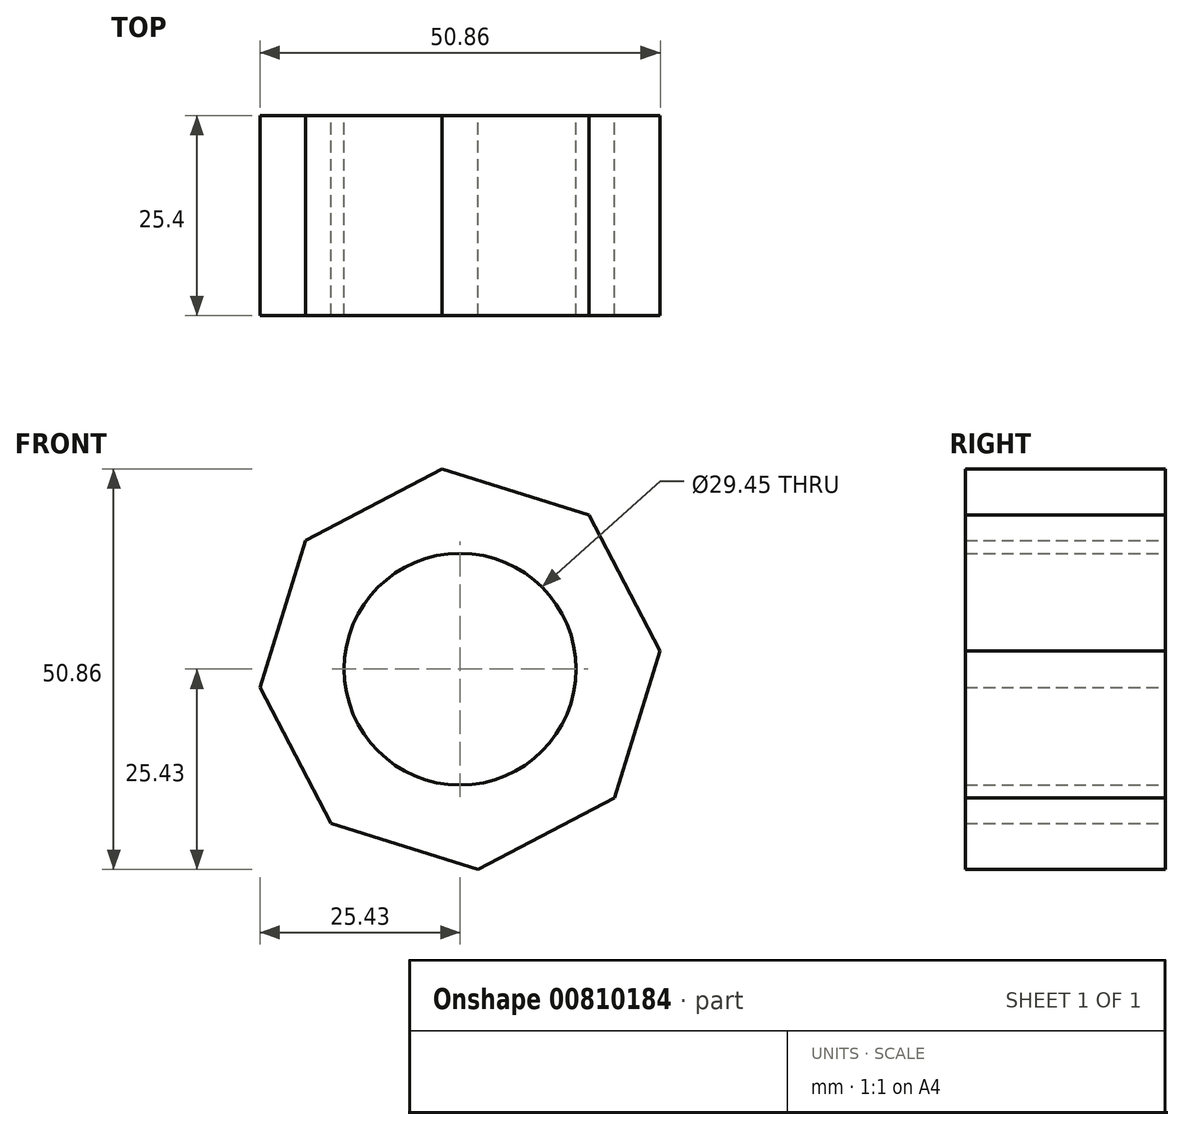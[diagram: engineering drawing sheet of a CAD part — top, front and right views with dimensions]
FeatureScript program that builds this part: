
annotation { "Feature Type Name" : "Feature", "Feature Type Description" : "" }
export const myFeature = defineFeature(function(context is Context, id is Id, definition is map)
    precondition{}
    {
        {
            var Q0;
            Q0=qCreatedBy(makeId("Front.planeOp"),FACE);
            var sketch = newSketch(context, id + "F0", { "sketchPlane" : qUnion([Q0])});
            skCircle(sketch, "E0.cCircle", {"center": v(0, 0) * mm, "radius": 23.59 * mm, "construction": true});
            skLineSegment(sketch, "E0.0", {"start": v(-25.43, -2.3) * mm, "end": v(-19.6, 16.35) * mm});
            skLineSegment(sketch, "E0.1", {"start": v(-19.6, 16.35) * mm, "end": v(-2.3, 25.43) * mm});
            skLineSegment(sketch, "E0.2", {"start": v(-2.3, 25.43) * mm, "end": v(16.35, 19.6) * mm});
            skLineSegment(sketch, "E0.3", {"start": v(16.35, 19.6) * mm, "end": v(25.43, 2.3) * mm});
            skLineSegment(sketch, "E0.4", {"start": v(25.43, 2.3) * mm, "end": v(19.6, -16.35) * mm});
            skLineSegment(sketch, "E0.5", {"start": v(19.6, -16.35) * mm, "end": v(2.3, -25.43) * mm});
            skLineSegment(sketch, "E0.6", {"start": v(2.3, -25.43) * mm, "end": v(-16.35, -19.6) * mm});
            skLineSegment(sketch, "E0.7", {"start": v(-16.35, -19.6) * mm, "end": v(-25.43, -2.3) * mm});
            skPoint(sketch, "E0.0.midPoint", {"position": v(-22.52, 7.03) * mm});
            skCircle(sketch, "E1", {"center": v(0, 0) * mm, "radius": 14.73 * mm});
            skSolve(sketch);
        }
        {
            var Q0;
            Q0 = qSketchRegion(id + "F0", true);
            extrude(context, id + "F1", {"entities" : qUnion([Q0]), "endBound" : BoundingType.SYMMETRIC, "depth" : 25.4 * mm, "offsetDistance" : 25.4 * mm});
        }
    });
